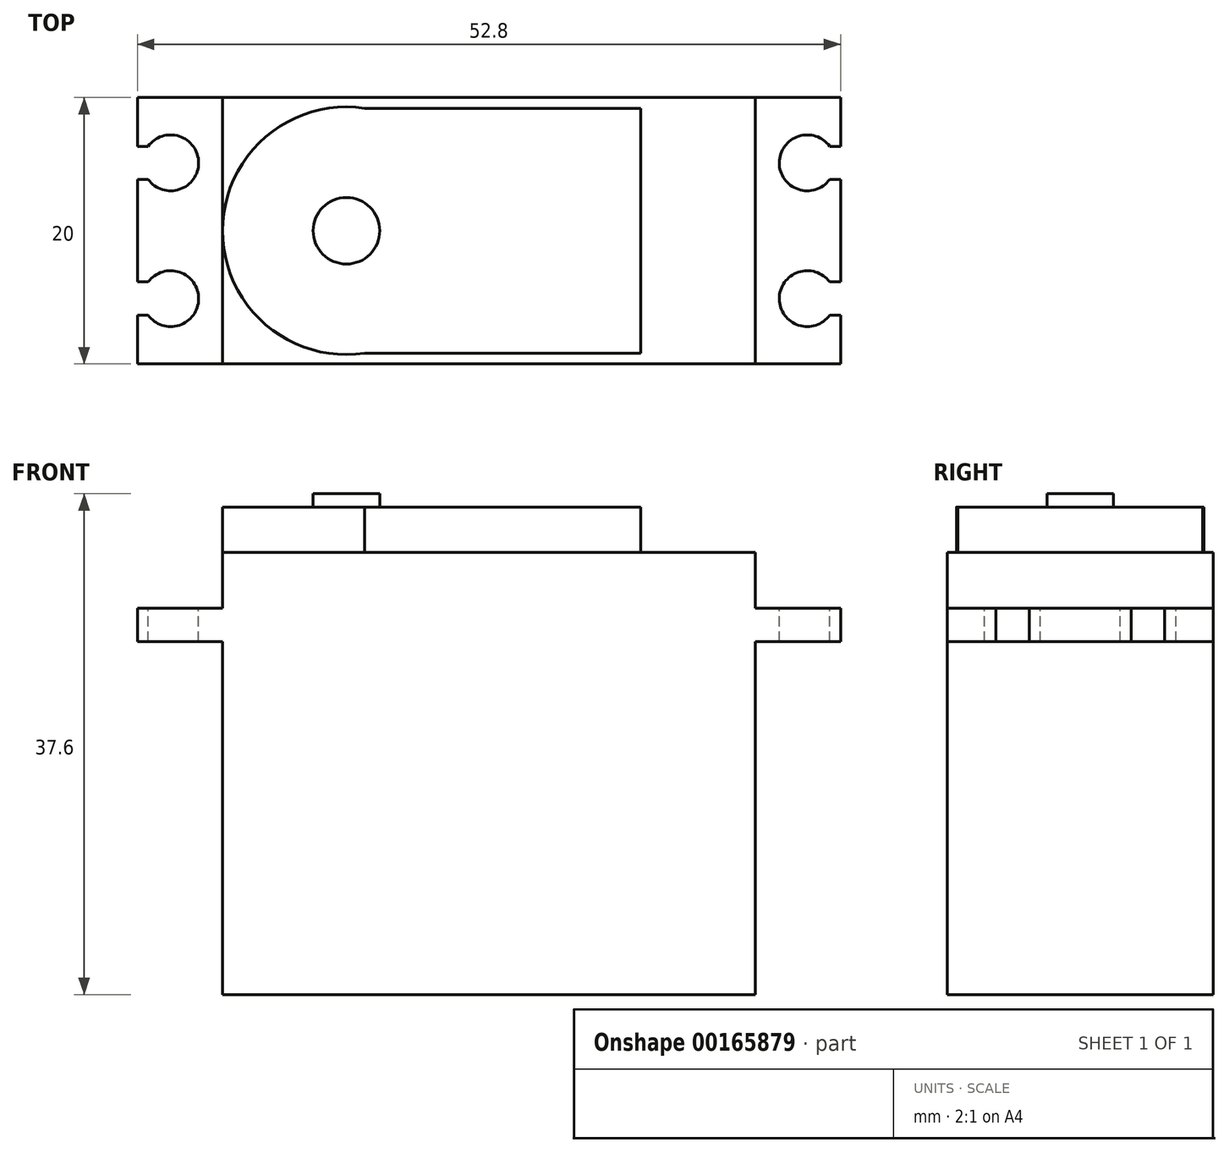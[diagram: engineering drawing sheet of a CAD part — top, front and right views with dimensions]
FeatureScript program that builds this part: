
annotation { "Feature Type Name" : "Feature", "Feature Type Description" : "" }
export const myFeature = defineFeature(function(context is Context, id is Id, definition is map)
    precondition{}
    {
        {
            var Q0;
            Q0=qCreatedBy(makeId("Top.planeOp"),FACE);
            var sketch = newSketch(context, id + "F0", { "sketchPlane" : qUnion([Q0])});
            skLineSegment(sketch, "E0.bottom", {"start": v(-432.7, -254) * mm, "end": v(432.7, -254) * mm});
            skLineSegment(sketch, "E0.top", {"start": v(-432.7, 254) * mm, "end": v(432.7, 254) * mm});
            skLineSegment(sketch, "E0.left", {"start": v(-432.7, -254) * mm, "end": v(-432.7, 254) * mm});
            skLineSegment(sketch, "E0.right", {"start": v(432.7, -254) * mm, "end": v(432.7, 254) * mm});
            skPoint(sketch, "E0.middle", {"position": v(0, 0) * mm});
            skLineSegment(sketch, "E1.bottom", {"start": v(20, -10) * mm, "end": v(-20, -10) * mm});
            skLineSegment(sketch, "E1.top", {"start": v(20, 10) * mm, "end": v(-20, 10) * mm});
            skLineSegment(sketch, "E1.left", {"start": v(20, -10) * mm, "end": v(20, 10) * mm});
            skLineSegment(sketch, "E1.right", {"start": v(-20, -10) * mm, "end": v(-20, 10) * mm});
            skSolve(sketch);
        }
        {
            var Q0;
            Q0=makeQuery(id+"F0.imprint","IMPRINT",FACE,{"disambiguationData":[TD([[makeQuery(id+"F0.imprint","IMPRINT",EDGE,{"derivedFrom":sQuery(id+"F0.wireOp",EDGE,"E1.bottom")}),-1.0]])]});
            extrude(context, id + "F1", {"entities" : qUnion([Q0]), "depth" : 26.5 * mm});
        }
        {
            var Q0;
            Q0=makeQuery(id+"F1.opExtrude","CAP_FACE",FACE,{"disambiguationData":[OSD([sQuery(id+"F0.wireOp",EDGE,"E1.bottom"),sQuery(id+"F0.wireOp",EDGE,"E1.top"),sQuery(id+"F0.wireOp",EDGE,"E1.left"),sQuery(id+"F0.wireOp",EDGE,"E1.right")])],"isStart":false});
            var sketch = newSketch(context, id + "F2", { "sketchPlane" : qUnion([Q0])});
            skLineSegment(sketch, "E2.bottom", {"start": v(26.4, -10) * mm, "end": v(-26.4, -10) * mm});
            skLineSegment(sketch, "E2.top", {"start": v(26.4, 10) * mm, "end": v(-26.4, 10) * mm});
            skLineSegment(sketch, "E2.left", {"start": v(26.4, -10) * mm, "end": v(26.4, 10) * mm});
            skLineSegment(sketch, "E2.right", {"start": v(-26.4, -10) * mm, "end": v(-26.4, 10) * mm});
            skPoint(sketch, "E2.middle", {"position": v(0, 0) * mm});
            skSolve(sketch);
        }
        {
            var Q0;
            Q0 = qSketchRegion(id + "F2", true);
            extrude(context, id + "F3", {"entities" : qUnion([Q0]), "operationType" : NewBodyOperationType.ADD, "depth" : 2.5 * mm});
        }
        {
            var Q0;
            Q0=makeQuery(id+"F3.opExtrude","CAP_FACE",FACE,{"disambiguationData":[OSD([sQuery(id+"F2.wireOp",EDGE,"E2.bottom"),sQuery(id+"F2.wireOp",EDGE,"E2.top"),sQuery(id+"F2.wireOp",EDGE,"E2.left"),sQuery(id+"F2.wireOp",EDGE,"E2.right")])],"isStart":false});
            var sketch = newSketch(context, id + "F4", { "sketchPlane" : qUnion([Q0])});
            skLineSegment(sketch, "E3.bottom", {"start": v(20, -10) * mm, "end": v(-20, -10) * mm});
            skLineSegment(sketch, "E3.top", {"start": v(20, 10) * mm, "end": v(-20, 10) * mm});
            skLineSegment(sketch, "E3.left", {"start": v(20, -10) * mm, "end": v(20, 10) * mm});
            skLineSegment(sketch, "E3.right", {"start": v(-20, -10) * mm, "end": v(-20, 10) * mm});
            skPoint(sketch, "E3.middle", {"position": v(0, 0) * mm});
            skSolve(sketch);
        }
        {
            var Q0;
            Q0=makeQuery(id+"F4.imprint","IMPRINT",FACE,{"disambiguationData":[TD([[makeQuery(id+"F4.imprint","IMPRINT",EDGE,{"derivedFrom":sQuery(id+"F4.wireOp",EDGE,"E3.bottom")}),-1.0]])]});
            extrude(context, id + "F5", {"entities" : qUnion([Q0]), "operationType" : NewBodyOperationType.ADD, "depth" : 4.2 * mm});
        }
        {
            var Q0;
            Q0=makeQuery(id+"F5.opExtrude","CAP_FACE",FACE,{"disambiguationData":[OSD([sQuery(id+"F4.wireOp",EDGE,"E3.bottom"),sQuery(id+"F4.wireOp",EDGE,"E3.top"),sQuery(id+"F4.wireOp",EDGE,"E3.left"),sQuery(id+"F4.wireOp",EDGE,"E3.right")])],"isStart":false});
            var sketch = newSketch(context, id + "F6", { "sketchPlane" : qUnion([Q0])});
            skCircle(sketch, "E4", {"center": v(-10.7, 0) * mm, "radius": 9.3 * mm});
            skLineSegment(sketch, "E5.bottom", {"start": v(-10.7, 9.2) * mm, "end": v(11.4, 9.2) * mm});
            skLineSegment(sketch, "E5.top", {"start": v(-10.7, -9.2) * mm, "end": v(11.4, -9.2) * mm});
            skLineSegment(sketch, "E5.left", {"start": v(-10.7, 9.2) * mm, "end": v(-10.7, -9.2) * mm});
            skLineSegment(sketch, "E5.right", {"start": v(11.4, 9.2) * mm, "end": v(11.4, -9.2) * mm});
            skSolve(sketch);
        }
        {
            var Q0;
            {var subQ0=sQuery(id+"F6.wireOp",EDGE,"E5.left");Q0=makeQuery(id+"F6.imprint","IMPRINT",FACE,{"disambiguationData":[TD([[makeQuery(id+"F6.imprint","IMPRINT",EDGE,{"derivedFrom":subQ0}),-1.0]])]});}
            var Q1;
            {var subQ5=sQuery(id+"F6.wireOp",EDGE,"E5.left");Q1=makeQuery(id+"F6.imprint","IMPRINT",FACE,{"disambiguationData":[TD([[makeQuery(id+"F6.imprint","IMPRINT",EDGE,{"derivedFrom":subQ5}),1.0]])]});}
            var Q2;
            {var subQ5=sQuery(id+"F6.wireOp",EDGE,"E5.right");Q2=makeQuery(id+"F6.imprint","IMPRINT",FACE,{"disambiguationData":[TD([[makeQuery(id+"F6.imprint","IMPRINT",EDGE,{"derivedFrom":subQ5}),-1.0]])]});}
            extrude(context, id + "F7", {"entities" : qUnion([Q0, Q1, Q2]), "operationType" : NewBodyOperationType.ADD, "depth" : 3.4 * mm});
        }
        {
            var Q0;
            Q0=makeQuery(id+"F7.opExtrude","CAP_FACE",FACE,{"disambiguationData":[OSD([sQuery(id+"F6.wireOp",EDGE,"E4"),sQuery(id+"F6.wireOp",EDGE,"E5.bottom"),sQuery(id+"F6.wireOp",EDGE,"E5.top"),sQuery(id+"F6.wireOp",EDGE,"E5.right")])],"isStart":false});
            var sketch = newSketch(context, id + "F8", { "sketchPlane" : qUnion([Q0])});
            skCircle(sketch, "E6", {"center": v(-10.7, 0) * mm, "radius": 2.5 * mm});
            skSolve(sketch);
        }
        {
            var Q0;
            Q0=makeQuery(id+"F8.imprint","IMPRINT",FACE,{"disambiguationData":[TD([[makeQuery(id+"F8.imprint","IMPRINT",EDGE,{"derivedFrom":sQuery(id+"F8.wireOp",EDGE,"E6")}),1.0]])]});
            extrude(context, id + "F9", {"entities" : qUnion([Q0]), "operationType" : NewBodyOperationType.ADD, "depth" : 1 * mm});
        }
        {
            var Q0;
            {var subQ0=sQuery(id+"F2.wireOp",EDGE,"E2.top");var subQ1=sQuery(id+"F2.wireOp",EDGE,"E2.bottom");var subQ2=sQuery(id+"F2.wireOp",EDGE,"E2.right");Q0=makeQuery(id+"F5.boolean.opBoolean","SPLIT",FACE,{"disambiguationData":[TD([makeQuery(id+"F3.opExtrude","SWEPT_FACE",FACE,{"disambiguationData":[OSD([subQ2])]})])],"derivedFrom":makeQuery(id+"F3.opExtrude","CAP_FACE",FACE,{"disambiguationData":[OSD([subQ1,subQ0,sQuery(id+"F2.wireOp",EDGE,"E2.left"),subQ2])],"isStart":false})});}
            var sketch = newSketch(context, id + "F10", { "sketchPlane" : qUnion([Q0])});
            skLineSegment(sketch, "E7.bottom", {"start": v(-23.9, 5.1) * mm, "end": v(23.9, 5.1) * mm});
            skLineSegment(sketch, "E7.top", {"start": v(-23.9, -5.1) * mm, "end": v(23.9, -5.1) * mm});
            skLineSegment(sketch, "E7.left", {"start": v(-23.9, 5.1) * mm, "end": v(-23.9, -5.1) * mm});
            skLineSegment(sketch, "E7.right", {"start": v(23.9, 5.1) * mm, "end": v(23.9, -5.1) * mm});
            skPoint(sketch, "E7.middle", {"position": v(0, 0) * mm});
            skCircle(sketch, "E8", {"center": v(-23.9, 5.1) * mm, "radius": 2.1 * mm});
            skCircle(sketch, "E9", {"center": v(-23.9, -5.1) * mm, "radius": 2.1 * mm});
            skCircle(sketch, "E10", {"center": v(23.9, 5.1) * mm, "radius": 2.1 * mm});
            skCircle(sketch, "E11", {"center": v(23.9, -5.1) * mm, "radius": 2.1 * mm});
            skLineSegment(sketch, "E12.bottom", {"start": v(-27.25, 3.84) * mm, "end": v(-24.75, 3.84) * mm});
            skLineSegment(sketch, "E12.top", {"start": v(-27.25, 6.34) * mm, "end": v(-24.75, 6.34) * mm});
            skLineSegment(sketch, "E12.left", {"start": v(-27.25, 3.84) * mm, "end": v(-27.25, 6.34) * mm});
            skLineSegment(sketch, "E12.right", {"start": v(-24.75, 3.84) * mm, "end": v(-24.75, 6.34) * mm});
            skPoint(sketch, "E12.middle", {"position": v(-26, 5.09) * mm});
            skLineSegment(sketch, "E13.bottom", {"start": v(-27.25, -6.34) * mm, "end": v(-24.75, -6.34) * mm});
            skLineSegment(sketch, "E13.top", {"start": v(-27.25, -3.84) * mm, "end": v(-24.75, -3.84) * mm});
            skLineSegment(sketch, "E13.left", {"start": v(-27.25, -6.34) * mm, "end": v(-27.25, -3.84) * mm});
            skLineSegment(sketch, "E13.right", {"start": v(-24.75, -6.34) * mm, "end": v(-24.75, -3.84) * mm});
            skPoint(sketch, "E13.middle", {"position": v(-26, -5.09) * mm});
            skLineSegment(sketch, "E14.bottom", {"start": v(27.25, 3.84) * mm, "end": v(24.75, 3.84) * mm});
            skLineSegment(sketch, "E14.top", {"start": v(27.25, 6.34) * mm, "end": v(24.75, 6.34) * mm});
            skLineSegment(sketch, "E14.left", {"start": v(27.25, 3.84) * mm, "end": v(27.25, 6.34) * mm});
            skLineSegment(sketch, "E14.right", {"start": v(24.75, 3.84) * mm, "end": v(24.75, 6.34) * mm});
            skPoint(sketch, "E14.middle", {"position": v(26, 5.09) * mm});
            skLineSegment(sketch, "E15.bottom", {"start": v(27.25, -6.34) * mm, "end": v(24.75, -6.34) * mm});
            skLineSegment(sketch, "E15.top", {"start": v(27.25, -3.84) * mm, "end": v(24.75, -3.84) * mm});
            skLineSegment(sketch, "E15.left", {"start": v(27.25, -6.34) * mm, "end": v(27.25, -3.84) * mm});
            skLineSegment(sketch, "E15.right", {"start": v(24.75, -6.34) * mm, "end": v(24.75, -3.84) * mm});
            skPoint(sketch, "E15.middle", {"position": v(26, -5.09) * mm});
            skSolve(sketch);
        }
        {
            var Q0;
            {var subQ10=sQuery(id+"F10.wireOp",EDGE,"E12.right");Q0=makeQuery(id+"F10.imprint","IMPRINT",FACE,{"disambiguationData":[TD([[makeQuery(id+"F10.imprint","IMPRINT",EDGE,{"derivedFrom":subQ10}),-1.0]])]});}
            var Q1;
            {var subQ0=sQuery(id+"F10.wireOp",EDGE,"E7.left");var subQ1=sQuery(id+"F10.wireOp",EDGE,"E7.bottom");var subQ2=makeQuery(id+"F10.imprint","INTERSECT",VERTEX,{"derivedFrom":[subQ1,subQ0]});Q1=makeQuery(id+"F10.imprint","IMPRINT",FACE,{"disambiguationData":[TD([[makeQuery(id+"F10.imprint","IMPRINT",EDGE,{"disambiguationData":[TD([[subQ2,-1.0]])],"derivedFrom":subQ1}),-1.0]])]});}
            var Q2;
            {var subQ5=sQuery(id+"F10.wireOp",EDGE,"E12.right");Q2=makeQuery(id+"F10.imprint","IMPRINT",FACE,{"disambiguationData":[TD([[makeQuery(id+"F10.imprint","IMPRINT",EDGE,{"derivedFrom":subQ5}),1.0]])]});}
            var Q3;
            {var subQ10=sQuery(id+"F10.wireOp",EDGE,"E13.right");Q3=makeQuery(id+"F10.imprint","IMPRINT",FACE,{"disambiguationData":[TD([[makeQuery(id+"F10.imprint","IMPRINT",EDGE,{"derivedFrom":subQ10}),-1.0]])]});}
            var Q4;
            {var subQ0=sQuery(id+"F10.wireOp",EDGE,"E7.left");var subQ1=sQuery(id+"F10.wireOp",EDGE,"E7.top");var subQ2=makeQuery(id+"F10.imprint","INTERSECT",VERTEX,{"derivedFrom":[subQ1,subQ0]});Q4=makeQuery(id+"F10.imprint","IMPRINT",FACE,{"disambiguationData":[TD([[makeQuery(id+"F10.imprint","IMPRINT",EDGE,{"disambiguationData":[TD([[subQ2,-1.0]])],"derivedFrom":subQ1}),1.0]])]});}
            var Q5;
            {var subQ5=sQuery(id+"F10.wireOp",EDGE,"E13.right");Q5=makeQuery(id+"F10.imprint","IMPRINT",FACE,{"disambiguationData":[TD([[makeQuery(id+"F10.imprint","IMPRINT",EDGE,{"derivedFrom":subQ5}),1.0]])]});}
            var Q6;
            {var subQ5=sQuery(id+"F10.wireOp",EDGE,"E14.right");Q6=makeQuery(id+"F10.imprint","IMPRINT",FACE,{"disambiguationData":[TD([[makeQuery(id+"F10.imprint","IMPRINT",EDGE,{"derivedFrom":subQ5}),-1.0]])]});}
            var Q7;
            {var subQ5=sQuery(id+"F10.wireOp",EDGE,"E14.right");Q7=makeQuery(id+"F10.imprint","IMPRINT",FACE,{"disambiguationData":[TD([[makeQuery(id+"F10.imprint","IMPRINT",EDGE,{"derivedFrom":subQ5}),1.0]])]});}
            var Q8;
            {var subQ0=sQuery(id+"F10.wireOp",EDGE,"E7.right");var subQ1=sQuery(id+"F10.wireOp",EDGE,"E7.bottom");var subQ2=makeQuery(id+"F10.imprint","INTERSECT",VERTEX,{"derivedFrom":[subQ1,subQ0]});Q8=makeQuery(id+"F10.imprint","IMPRINT",FACE,{"disambiguationData":[TD([[makeQuery(id+"F10.imprint","IMPRINT",EDGE,{"disambiguationData":[TD([[subQ2,1.0]])],"derivedFrom":subQ1}),-1.0]])]});}
            var Q9;
            {var subQ5=sQuery(id+"F10.wireOp",EDGE,"E14.left");Q9=makeQuery(id+"F10.imprint","IMPRINT",FACE,{"disambiguationData":[TD([[makeQuery(id+"F10.imprint","IMPRINT",EDGE,{"derivedFrom":subQ5}),1.0]])]});}
            var Q10;
            {var subQ5=sQuery(id+"F10.wireOp",EDGE,"E15.left");Q10=makeQuery(id+"F10.imprint","IMPRINT",FACE,{"disambiguationData":[TD([[makeQuery(id+"F10.imprint","IMPRINT",EDGE,{"derivedFrom":subQ5}),1.0]])]});}
            var Q11;
            {var subQ5=sQuery(id+"F10.wireOp",EDGE,"E15.right");Q11=makeQuery(id+"F10.imprint","IMPRINT",FACE,{"disambiguationData":[TD([[makeQuery(id+"F10.imprint","IMPRINT",EDGE,{"derivedFrom":subQ5}),1.0]])]});}
            var Q12;
            {var subQ0=sQuery(id+"F10.wireOp",EDGE,"E7.right");var subQ1=sQuery(id+"F10.wireOp",EDGE,"E7.top");var subQ2=makeQuery(id+"F10.imprint","INTERSECT",VERTEX,{"derivedFrom":[subQ1,subQ0]});Q12=makeQuery(id+"F10.imprint","IMPRINT",FACE,{"disambiguationData":[TD([[makeQuery(id+"F10.imprint","IMPRINT",EDGE,{"disambiguationData":[TD([[subQ2,1.0]])],"derivedFrom":subQ1}),1.0]])]});}
            var Q13;
            {var subQ5=sQuery(id+"F10.wireOp",EDGE,"E15.right");Q13=makeQuery(id+"F10.imprint","IMPRINT",FACE,{"disambiguationData":[TD([[makeQuery(id+"F10.imprint","IMPRINT",EDGE,{"derivedFrom":subQ5}),-1.0]])]});}
            var Q14;
            {var subQ0=sQuery(id+"F10.wireOp",EDGE,"E13.top");var subQ1=sQuery(id+"F10.wireOp",EDGE,"E9");var subQ2=makeQuery(id+"F10.imprint","INTERSECT",VERTEX,{"derivedFrom":[subQ1,subQ0]});Q14=makeQuery(id+"F10.imprint","IMPRINT",FACE,{"disambiguationData":[TD([[makeQuery(id+"F10.imprint","IMPRINT",EDGE,{"disambiguationData":[TD([[subQ2,-1.0]])],"derivedFrom":subQ1}),-1.0]])]});}
            var Q15;
            {var subQ0=sQuery(id+"F10.wireOp",EDGE,"E12.top");var subQ1=sQuery(id+"F10.wireOp",EDGE,"E8");var subQ2=makeQuery(id+"F10.imprint","INTERSECT",VERTEX,{"derivedFrom":[subQ1,subQ0]});Q15=makeQuery(id+"F10.imprint","IMPRINT",FACE,{"disambiguationData":[TD([[makeQuery(id+"F10.imprint","IMPRINT",EDGE,{"disambiguationData":[TD([[subQ2,-1.0]])],"derivedFrom":subQ1}),-1.0]])]});}
            extrude(context, id + "F11", {"entities" : qUnion([Q0, Q1, Q2, Q3, Q4, Q5, Q6, Q7, Q8, Q9, Q10, Q11, Q12, Q13, Q14, Q15]), "operationType" : NewBodyOperationType.REMOVE, "endBound" : BoundingType.THROUGH_ALL, "oppositeDirection" : true, "depth" : 25 * mm});
        }
    });
